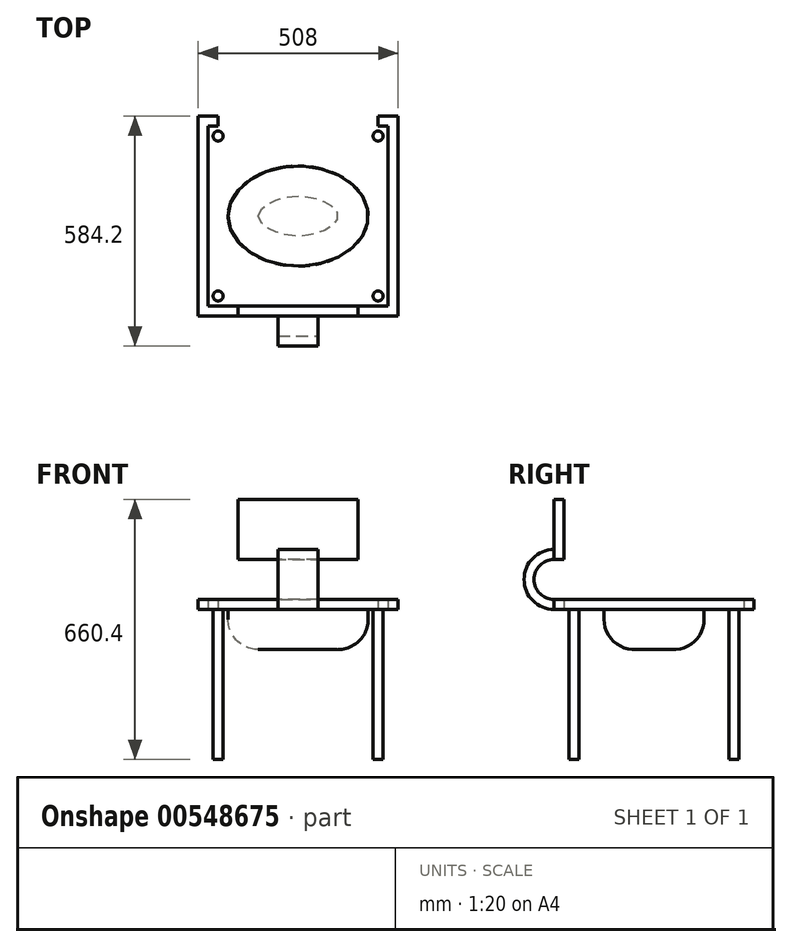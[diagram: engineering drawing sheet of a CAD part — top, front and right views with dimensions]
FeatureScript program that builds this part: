
annotation { "Feature Type Name" : "Feature", "Feature Type Description" : "" }
export const myFeature = defineFeature(function(context is Context, id is Id, definition is map)
    precondition{}
    {
        {
            var Q0;
            Q0=qCreatedBy(makeId("Top.planeOp"),FACE);
            var sketch = newSketch(context, id + "F0", { "sketchPlane" : qUnion([Q0])});
            skCircle(sketch, "E0", {"center": v(203.2, 0) * mm, "radius": 12.7 * mm});
            skCircle(sketch, "E1", {"center": v(-203.2, 0) * mm, "radius": 12.7 * mm});
            skLineSegment(sketch, "E2", {"start": v(0, 0) * mm, "end": v(0, -203.2) * mm});
            skLineSegment(sketch, "E3", {"start": v(0, -203.2) * mm, "end": v(-51.7, -203.2) * mm});
            skCircle(sketch, "E4.MirrorC", {"center": v(-203.2, -406.4) * mm, "radius": 12.7 * mm});
            skCircle(sketch, "E5.MirrorC", {"center": v(203.2, -406.4) * mm, "radius": 12.7 * mm});
            skSolve(sketch);
        }
        {
            var Q0;
            Q0 = qSketchRegion(id + "F0", true);
            extrude(context, id + "F1", {"entities" : qUnion([Q0]), "depth" : 381 * mm, "offsetDistance" : 25.4 * mm});
        }
        {
            var Q0;
            Q0=makeQuery(id+"F1.opExtrude","CAP_FACE",FACE,{"disambiguationData":[OSD([sQuery(id+"F0.wireOp",EDGE,"E4.MirrorC")])],"isStart":false});
            var sketch = newSketch(context, id + "F2", { "sketchPlane" : qUnion([Q0])});
            skLineSegment(sketch, "E6", {"start": v(-203.2, 50.8) * mm, "end": v(-254, 50.8) * mm});
            skLineSegment(sketch, "E7", {"start": v(203.2, 50.8) * mm, "end": v(254, 50.8) * mm});
            skLineSegment(sketch, "E8.left", {"start": v(-254, -457.2) * mm, "end": v(-254, 50.8) * mm});
            skLineSegment(sketch, "E8.right", {"start": v(254, -457.2) * mm, "end": v(254, 50.8) * mm});
            skLineSegment(sketch, "E9.bottom", {"start": v(-228.6, -431.8) * mm, "end": v(228.6, -431.8) * mm});
            skLineSegment(sketch, "E9.left", {"start": v(-228.6, -431.8) * mm, "end": v(-228.6, 25.4) * mm});
            skLineSegment(sketch, "E9.right", {"start": v(228.6, -431.8) * mm, "end": v(228.6, 25.4) * mm});
            skLineSegment(sketch, "E10", {"start": v(-228.6, 25.4) * mm, "end": v(-203.2, 25.4) * mm});
            skLineSegment(sketch, "E11", {"start": v(228.6, 25.4) * mm, "end": v(203.2, 25.4) * mm});
            skLineSegment(sketch, "E12", {"start": v(-203.2, 50.8) * mm, "end": v(-203.2, 25.4) * mm});
            skLineSegment(sketch, "E13", {"start": v(203.2, 25.4) * mm, "end": v(203.2, 50.8) * mm});
            skLineSegment(sketch, "E14", {"start": v(254, -457.2) * mm, "end": v(-254, -457.2) * mm});
            skSolve(sketch);
        }
        {
            var Q0;
            Q0=makeQuery(id+"F2.imprint","IMPRINT",FACE,{"disambiguationData":[TD([[makeQuery(id+"F2.imprint","IMPRINT",EDGE,{"derivedFrom":sQuery(id+"F2.wireOp",EDGE,"E6")}),1.0]])]});
            extrude(context, id + "F3", {"entities" : qUnion([Q0]), "depth" : 25.4 * mm, "offsetDistance" : 25.4 * mm});
        }
        {
            var Q0;
            Q0=makeQuery(id+"F3.opExtrude","CAP_FACE",FACE,{"disambiguationData":[OSD([sQuery(id+"F2.wireOp",EDGE,"E6"),sQuery(id+"F2.wireOp",EDGE,"E7"),sQuery(id+"F2.wireOp",EDGE,"E8.left"),sQuery(id+"F2.wireOp",EDGE,"E8.right"),sQuery(id+"F2.wireOp",EDGE,"E9.bottom"),sQuery(id+"F2.wireOp",EDGE,"E9.left"),sQuery(id+"F2.wireOp",EDGE,"E9.right"),sQuery(id+"F2.wireOp",EDGE,"E10"),sQuery(id+"F2.wireOp",EDGE,"E11"),sQuery(id+"F2.wireOp",EDGE,"E12"),sQuery(id+"F2.wireOp",EDGE,"E13"),sQuery(id+"F2.wireOp",EDGE,"E14")])],"isStart":true});
            var sketch = newSketch(context, id + "F4", { "sketchPlane" : qUnion([Q0])});
            skEllipse(sketch, "E15", {"center": v(0, 203.2) * mm, "majorRadius": 177.8 * mm, "minorRadius": 127 * mm, "majorAxis": v(-1, 0)});
            skSolve(sketch);
        }
        {
            var Q0;
            Q0=makeQuery(id+"F4.imprint","IMPRINT",FACE,{"disambiguationData":[TD([[makeQuery(id+"F4.imprint","IMPRINT",EDGE,{"derivedFrom":sQuery(id+"F4.wireOp",EDGE,"E15")}),1.0]])]});
            var Q1;
            Q1 = qSketchRegion(id + "F7", true);
            extrude(context, id + "F5", {"entities" : qUnion([Q0, Q1]), "depth" : 101.6 * mm, "offsetDistance" : 25.4 * mm});
        }
        {
            var Q0;
            Q0=makeQuery(id+"F5.opExtrude","CAP_EDGE",EDGE,{"disambiguationData":[OSD([sQuery(id+"F4.wireOp",EDGE,"E15")])],"isStart":false});
            fillet(context, id + "F6", {"entities" : qUnion([Q0]), "radius" : 76.2 * mm, "tangentPropagation" : true, "allowEdgeOverflow" : false});
        }
        {
            var Q0;
            Q0=makeQuery(id+"F3.opExtrude","SWEPT_FACE",FACE,{"disambiguationData":[OSD([sQuery(id+"F2.wireOp",EDGE,"E14")])]});
            var sketch = newSketch(context, id + "F7", { "sketchPlane" : qUnion([Q0])});
            skLineSegment(sketch, "E16.bottom", {"start": v(-50.8, 381) * mm, "end": v(50.8, 381) * mm});
            skLineSegment(sketch, "E16.top", {"start": v(-50.8, 406.4) * mm, "end": v(50.8, 406.4) * mm});
            skLineSegment(sketch, "E16.left", {"start": v(-50.8, 406.4) * mm, "end": v(-50.8, 381) * mm});
            skLineSegment(sketch, "E16.right", {"start": v(50.8, 406.4) * mm, "end": v(50.8, 381) * mm});
            skLineSegment(sketch, "E17.bottom", {"start": v(-152.4, 660.4) * mm, "end": v(152.4, 660.4) * mm});
            skLineSegment(sketch, "E17.top", {"start": v(-152.4, 508) * mm, "end": v(152.4, 508) * mm});
            skLineSegment(sketch, "E17.left", {"start": v(-152.4, 660.4) * mm, "end": v(-152.4, 508) * mm});
            skLineSegment(sketch, "E17.right", {"start": v(152.4, 660.4) * mm, "end": v(152.4, 508) * mm});
            skLineSegment(sketch, "E18", {"start": v(-104.99, 457.2) * mm, "end": v(94.44, 457.2) * mm});
            skSolve(sketch);
        }
        {
            var Q0;
            Q0=makeQuery(id+"F7.imprint","IMPRINT",FACE,{"disambiguationData":[TD([[makeQuery(id+"F7.imprint","IMPRINT",EDGE,{"derivedFrom":sQuery(id+"F7.wireOp",EDGE,"E16.bottom")}),-1.0]])]});
            var Q1;
            Q1=sQuery(id+"F7.wireOp",EDGE,"E18");
            revolve(context, id + "F8", {"operationType" : NewBodyOperationType.ADD, "entities" : qUnion([Q0]), "axis" : qUnion([Q1]), "revolveType" : RevolveType.ONE_DIRECTION, "oppositeDirection" : true, "angle" : 180 * degree});
        }
        {
            var Q0;
            Q0=makeQuery(id+"F7.imprint","IMPRINT",FACE,{"disambiguationData":[TD([[makeQuery(id+"F7.imprint","IMPRINT",EDGE,{"derivedFrom":sQuery(id+"F7.wireOp",EDGE,"E17.bottom")}),-1.0]])]});
            extrude(context, id + "F9", {"entities" : qUnion([Q0]), "operationType" : NewBodyOperationType.ADD, "oppositeDirection" : true, "depth" : 25.4 * mm, "offsetDistance" : 25.4 * mm});
        }
    });
